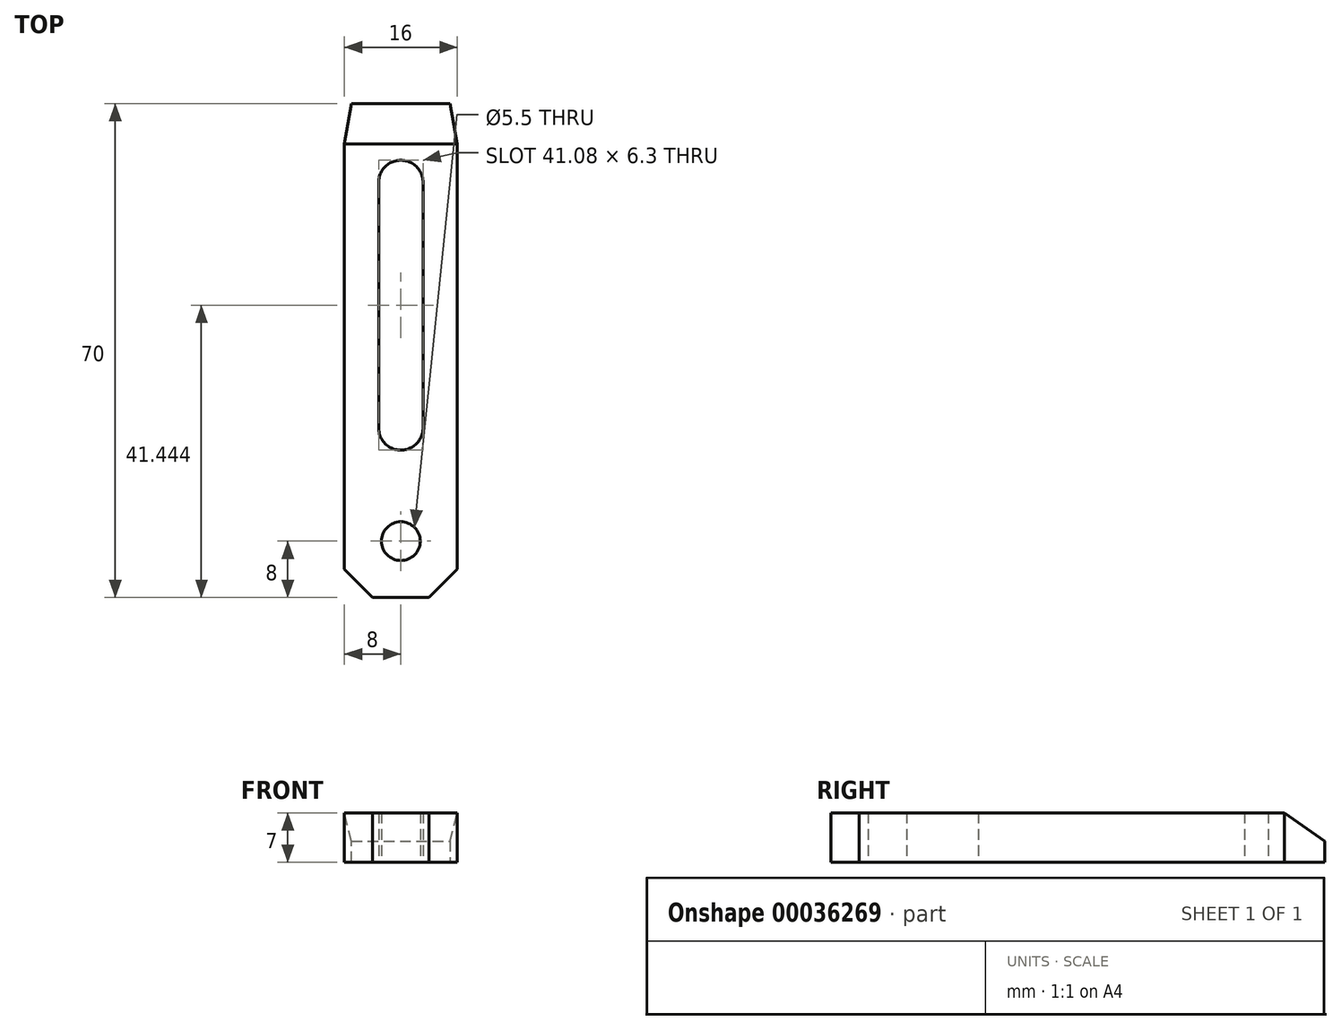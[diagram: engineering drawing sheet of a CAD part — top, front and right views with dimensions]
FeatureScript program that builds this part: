
annotation { "Feature Type Name" : "Feature", "Feature Type Description" : "" }
export const myFeature = defineFeature(function(context is Context, id is Id, definition is map)
    precondition{}
    {
        {
            var Q0;
            Q0=qCreatedBy(makeId("Top.planeOp"),FACE);
            var sketch = newSketch(context, id + "F0", { "sketchPlane" : qUnion([Q0])});
            skLineSegment(sketch, "E0.bottom", {"start": v(0, 0) * mm, "end": v(16, 0) * mm});
            skLineSegment(sketch, "E0.top", {"start": v(0, 70) * mm, "end": v(16, 70) * mm});
            skLineSegment(sketch, "E0.left", {"start": v(0, 0) * mm, "end": v(0, 70) * mm});
            skLineSegment(sketch, "E0.right", {"start": v(16, 0) * mm, "end": v(16, 70) * mm});
            skLineSegment(sketch, "E1", {"start": v(8, 0) * mm, "end": v(8, 70) * mm, "construction": true});
            skCircle(sketch, "E2", {"center": v(8, 8) * mm, "radius": 2.75 * mm});
            skArc(sketch, "E3", {"start": v(11.15, 58.83) * mm, "mid": v(7.89, 61.98) * mm, "end": v(4.86, 58.61) * mm});
            skArc(sketch, "E4", {"start": v(4.85, 24.06) * mm, "mid": v(8, 20.9) * mm, "end": v(11.15, 24.06) * mm});
            skLineSegment(sketch, "E5", {"start": v(4.86, 59.06) * mm, "end": v(4.85, 24.06) * mm});
            skLineSegment(sketch, "E6", {"start": v(11.15, 58.83) * mm, "end": v(11.15, 24.06) * mm});
            skSolve(sketch);
        }
        {
            var Q0;
            Q0=makeQuery(id+"F0.imprint","IMPRINT",FACE,{"disambiguationData":[TD([[makeQuery(id+"F0.imprint","IMPRINT",EDGE,{"derivedFrom":sQuery(id+"F0.wireOp",EDGE,"E0.bottom")}),1.0]])]});
            extrude(context, id + "F1", {"entities" : qUnion([Q0]), "flatOperationType" : FlatOperationType.REMOVE, "offsetDistance" : 25 * mm, "depth" : 7 * mm, "domain" : OperationDomain.MODEL});
        }
        {
            var Q0;
            Q0=makeQuery(id+"F1.opExtrude","CAP_EDGE",EDGE,{"disambiguationData":[OSD([sQuery(id+"F0.wireOp",EDGE,"E0.top")])],"isStart":false});
            chamfer(context, id + "F2", {"entities" : qUnion([Q0]), "chamferType" : ChamferType.OFFSET_ANGLE, "width" : 4 * mm, "oppositeDirection" : false, "angle" : 55 * degree, "tangentPropagation" : true});
        }
        {
            var Q0;
            Q0=makeQuery(id+"F1.opExtrude","SWEPT_EDGE",EDGE,{"disambiguationData":[OSD([sQuery(id+"F0.wireOp",EDGE,"E0.bottom"),sQuery(id+"F0.wireOp",EDGE,"E0.right")])]});
            var Q1;
            Q1=makeQuery(id+"F1.opExtrude","SWEPT_EDGE",EDGE,{"disambiguationData":[OSD([sQuery(id+"F0.wireOp",EDGE,"E0.bottom"),sQuery(id+"F0.wireOp",EDGE,"E0.left")])]});
            chamfer(context, id + "F3", {"entities" : qUnion([Q0, Q1]), "width" : 4 * mm, "tangentPropagation" : true});
        }
        {
            var Q0;
            Q0=makeQuery(id+"F1.opExtrude","SWEPT_EDGE",EDGE,{"disambiguationData":[OSD([sQuery(id+"F0.wireOp",EDGE,"E0.top"),sQuery(id+"F0.wireOp",EDGE,"E0.right")])]});
            var Q1;
            Q1=makeQuery(id+"F1.opExtrude","SWEPT_EDGE",EDGE,{"disambiguationData":[OSD([sQuery(id+"F0.wireOp",EDGE,"E0.top"),sQuery(id+"F0.wireOp",EDGE,"E0.left")])]});
            chamfer(context, id + "F4", {"entities" : qUnion([Q0, Q1]), "chamferType" : ChamferType.TWO_OFFSETS, "width1" : 1 * mm, "oppositeDirection" : false, "width2" : 5.7 * mm, "tangentPropagation" : true});
        }
    });
